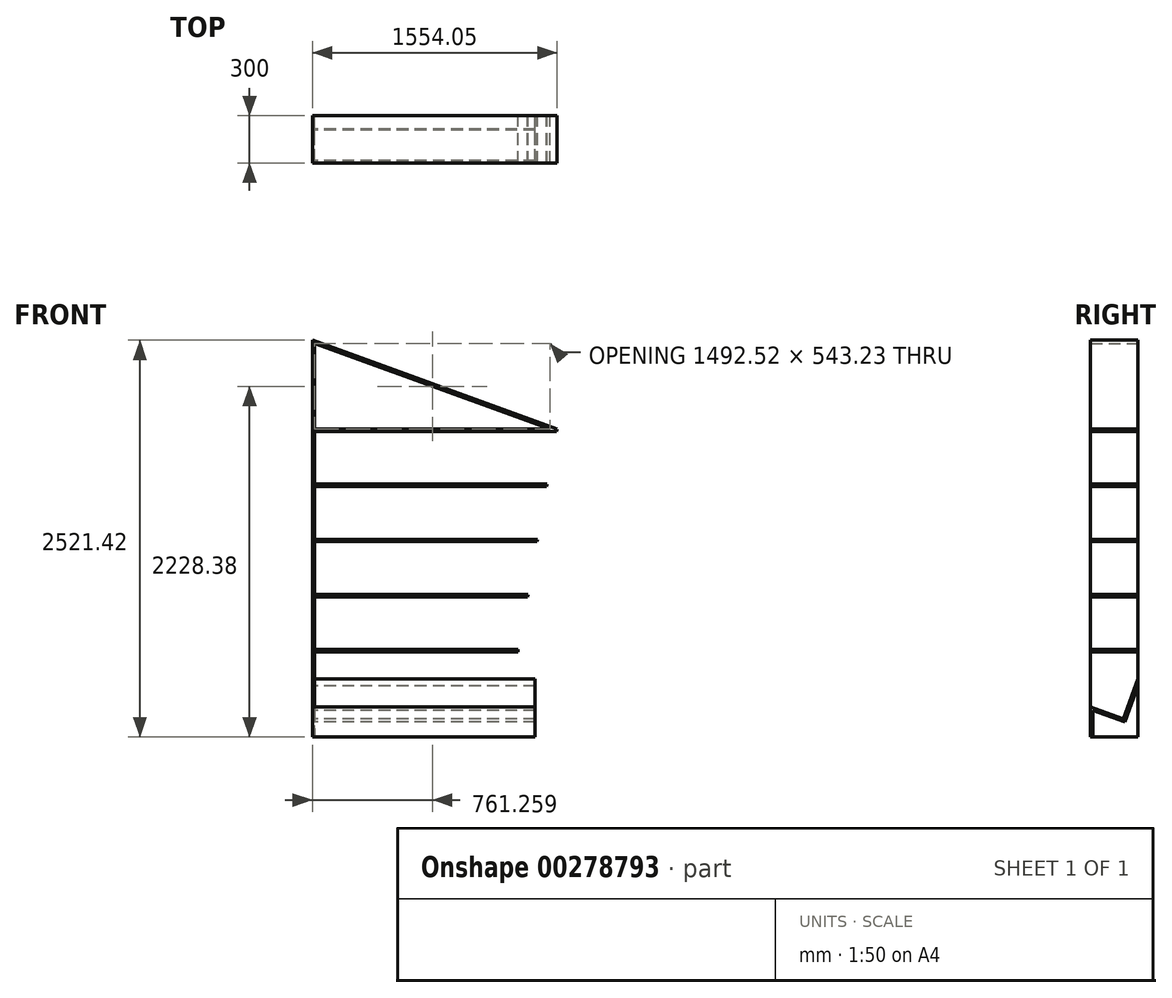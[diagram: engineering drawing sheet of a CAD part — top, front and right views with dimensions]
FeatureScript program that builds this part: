
annotation { "Feature Type Name" : "Feature", "Feature Type Description" : "" }
export const myFeature = defineFeature(function(context is Context, id is Id, definition is map)
    precondition{}
    {
        {
            var Q0;
            Q0=qCreatedBy(makeId("Front.planeOp"),FACE);
            var sketch = newSketch(context, id + "F0", { "sketchPlane" : qUnion([Q0])});
            skLineSegment(sketch, "E0", {"start": v(15, 0) * mm, "end": v(15, 2500) * mm});
            skLineSegment(sketch, "E1", {"start": v(15, 2500) * mm, "end": v(1548.73, 1941.77) * mm});
            skLineSegment(sketch, "E2", {"start": v(1515, 0) * mm, "end": v(15, 0) * mm, "construction": true});
            skLineSegment(sketch, "E3", {"start": v(1548.73, 1941.77) * mm, "end": v(1210.06, 0) * mm, "construction": true});
            skLineSegment(sketch, "E4", {"start": v(1548.73, 1941.77) * mm, "end": v(15, 1941.77) * mm});
            skLineSegment(sketch, "E5", {"start": v(15, 1591.77) * mm, "end": v(1487.69, 1591.77) * mm});
            skLineSegment(sketch, "E6", {"start": v(15, 1241.77) * mm, "end": v(1426.64, 1241.77) * mm});
            skLineSegment(sketch, "E7", {"start": v(15, 1941.77) * mm, "end": v(15, 1591.77) * mm});
            skLineSegment(sketch, "E8", {"start": v(15, 1591.77) * mm, "end": v(15, 1241.77) * mm});
            skLineSegment(sketch, "E9", {"start": v(15, 1241.77) * mm, "end": v(15, 891.77) * mm});
            skLineSegment(sketch, "E10", {"start": v(15, 891.77) * mm, "end": v(1365.6, 891.77) * mm});
            skLineSegment(sketch, "E11", {"start": v(15, 891.77) * mm, "end": v(15, 541.77) * mm});
            skLineSegment(sketch, "E12", {"start": v(15, 541.77) * mm, "end": v(1304.55, 541.77) * mm});
            skLineSegment(sketch, "E13.0", {"start": v(0, 2521.42) * mm, "end": v(1554.05, 1955.8) * mm});
            skLineSegment(sketch, "E13.1", {"start": v(0, 0) * mm, "end": v(0, 2521.42) * mm});
            skLineSegment(sketch, "E14", {"start": v(0, 0) * mm, "end": v(15, 0) * mm});
            skLineSegment(sketch, "E15", {"start": v(15, 541.77) * mm, "end": v(15, 556.77) * mm});
            skLineSegment(sketch, "E16", {"start": v(1507.52, 1956.77) * mm, "end": v(15, 1956.77) * mm});
            skLineSegment(sketch, "E17", {"start": v(15, 1606.77) * mm, "end": v(1490.3, 1606.77) * mm});
            skLineSegment(sketch, "E18", {"start": v(15, 1256.77) * mm, "end": v(1429.26, 1256.77) * mm});
            skLineSegment(sketch, "E19", {"start": v(15, 906.77) * mm, "end": v(1368.21, 906.77) * mm});
            skLineSegment(sketch, "E20", {"start": v(15, 556.77) * mm, "end": v(1307.17, 556.77) * mm});
            skLineSegment(sketch, "E21", {"start": v(15, 906.77) * mm, "end": v(15, 891.77) * mm});
            skLineSegment(sketch, "E22", {"start": v(15, 1256.77) * mm, "end": v(15, 1241.77) * mm});
            skLineSegment(sketch, "E23", {"start": v(15, 1606.77) * mm, "end": v(15, 1591.77) * mm});
            skLineSegment(sketch, "E24", {"start": v(15, 1956.77) * mm, "end": v(15, 1941.77) * mm});
            skLineSegment(sketch, "E25", {"start": v(1554.05, 1955.8) * mm, "end": v(1548.73, 1941.77) * mm});
            skLineSegment(sketch, "E26", {"start": v(1304.55, 541.77) * mm, "end": v(1307.17, 556.77) * mm});
            skLineSegment(sketch, "E27", {"start": v(1365.6, 891.77) * mm, "end": v(1368.21, 906.77) * mm});
            skLineSegment(sketch, "E28", {"start": v(1426.64, 1241.77) * mm, "end": v(1429.26, 1256.77) * mm});
            skLineSegment(sketch, "E29", {"start": v(1487.69, 1591.77) * mm, "end": v(1490.3, 1606.77) * mm});
            skSolve(sketch);
        }
        {
            var Q0;
            Q0 = qSketchRegion(id + "F0", true);
            extrude(context, id + "F1", {"entities" : qUnion([Q0]), "depth" : 300 * mm});
        }
        {
            var Q0;
            {var subQ0=sQuery(id+"F0.wireOp",EDGE,"E0");Q0=makeQuery(id+"F1.opExtrude","SWEPT_FACE",FACE,{"disambiguationData":[OSD([subQ0]),TDD([makeQuery(id+"F0.imprint","IMPRINT",EDGE,{"disambiguationData":[TD([[makeQuery(id+"F0.imprint","INTERSECT",VERTEX,{"derivedFrom":[subQ0,sQuery(id+"F0.wireOp",EDGE,"E14")]}),-1.0]])],"derivedFrom":subQ0})])]});}
            var sketch = newSketch(context, id + "F2", { "sketchPlane" : qUnion([Q0])});
            skLineSegment(sketch, "E30", {"start": v(-300, 191.77) * mm, "end": v(-91.85, 116) * mm});
            skLineSegment(sketch, "E31", {"start": v(-91.85, 116) * mm, "end": v(0, 368.35) * mm});
            skLineSegment(sketch, "E32", {"start": v(-285, 170.35) * mm, "end": v(-82.88, 96.78) * mm});
            skLineSegment(sketch, "E33", {"start": v(-82.88, 96.78) * mm, "end": v(0, 324.5) * mm});
            skLineSegment(sketch, "E34", {"start": v(-285, 170.35) * mm, "end": v(-285, 0) * mm});
            skLineSegment(sketch, "E35", {"start": v(0, 368.35) * mm, "end": v(0, 324.5) * mm});
            skLineSegment(sketch, "E36", {"start": v(-300, 191.77) * mm, "end": v(-300, 0) * mm});
            skLineSegment(sketch, "E37", {"start": v(-300, 0) * mm, "end": v(-285, 0) * mm});
            skSolve(sketch);
        }
        {
            var Q0;
            Q0 = qSketchRegion(id + "F2", true);
            extrude(context, id + "F3", {"entities" : qUnion([Q0]), "operationType" : NewBodyOperationType.ADD, "depth" : 1400 * mm});
        }
    });
